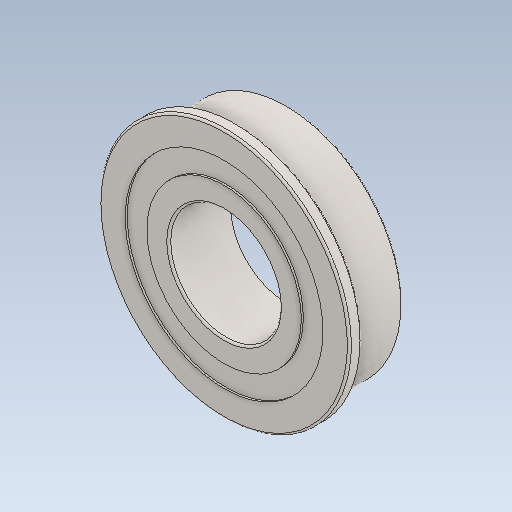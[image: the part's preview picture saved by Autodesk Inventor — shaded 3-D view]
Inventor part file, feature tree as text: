
AUTODESK INVENTOR PART (.ipt)
format: ipt  version: 2020 (Build 240168000, 168)  size: 219,136 bytes
history: native  units: in
note: dims shown in document units (in); Inventor stores cm internally (conversion verified against a paired STEP export)
features: fillet x1
ambient origin geometry x8: Origin, YZ Plane, XZ Plane, XY Plane, X Axis, Y Axis, Z Axis, Center Point
bodies: Solid1 (feature_tree)
feature tree (1):
  fillet  "Fillet1"  [1 undecoded]
note: 1 required parameter value undecoded (feature->parameter linkage not recoverable at this tier; creation-order binding heuristic only, values carry confidence <= 0.55)
